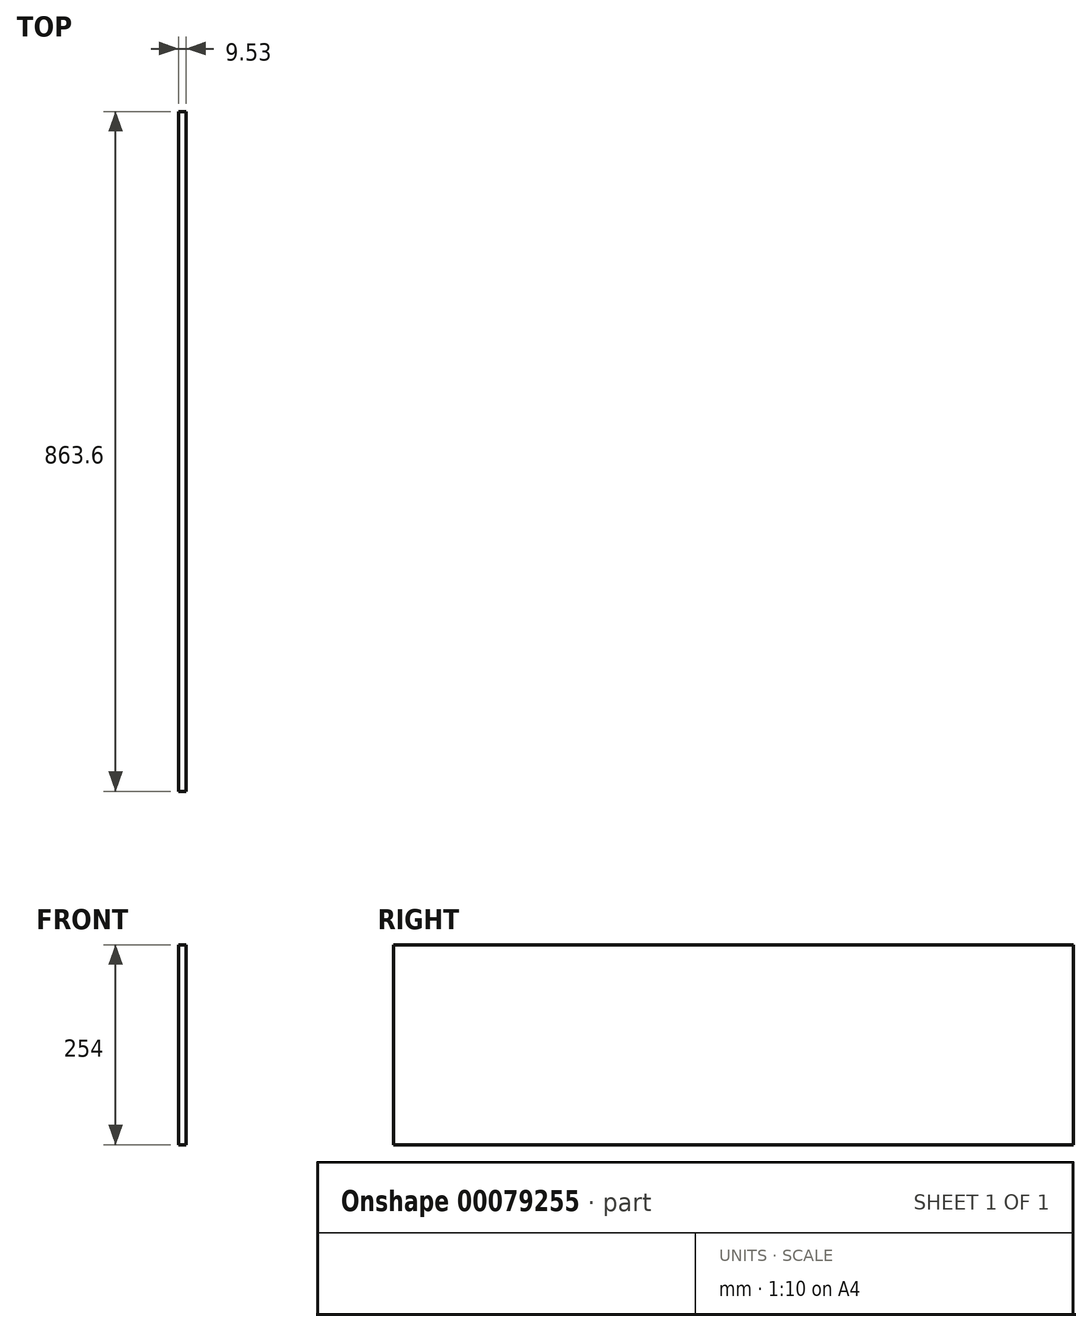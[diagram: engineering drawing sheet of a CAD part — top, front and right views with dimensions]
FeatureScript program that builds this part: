
annotation { "Feature Type Name" : "Feature", "Feature Type Description" : "" }
export const myFeature = defineFeature(function(context is Context, id is Id, definition is map)
    precondition{}
    {
        {
            var Q0;
            Q0=qCreatedBy(makeId("Right.planeOp"),FACE);
            var sketch = newSketch(context, id + "F0", { "sketchPlane" : qUnion([Q0])});
            skLineSegment(sketch, "E0.bottom", {"start": v(0, 0) * mm, "end": v(863.6, 0) * mm});
            skLineSegment(sketch, "E0.top", {"start": v(0, 254) * mm, "end": v(863.6, 254) * mm});
            skLineSegment(sketch, "E0.left", {"start": v(0, 0) * mm, "end": v(0, 254) * mm});
            skLineSegment(sketch, "E0.right", {"start": v(863.6, 0) * mm, "end": v(863.6, 254) * mm});
            skSolve(sketch);
        }
        {
            var Q0;
            Q0=makeQuery(id+"F0.imprint","IMPRINT",FACE,{"disambiguationData":[TD([[makeQuery(id+"F0.imprint","IMPRINT",EDGE,{"derivedFrom":sQuery(id+"F0.wireOp",EDGE,"E0.bottom")}),1.0]])]});
            extrude(context, id + "F1", {"entities" : qUnion([Q0]), "depth" : 9.52 * mm});
        }
    });
